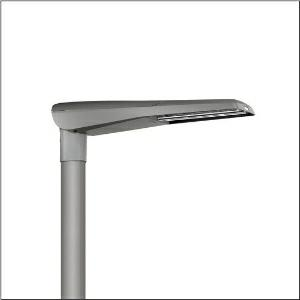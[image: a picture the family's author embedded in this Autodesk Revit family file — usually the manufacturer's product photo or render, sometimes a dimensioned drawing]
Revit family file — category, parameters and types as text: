
# Revit family: streetlight_sl_11_iq_mini___st0_5a_5xc2bc1f08ge_6b58
name_source: partatom
category: Lighting Fixtures
units: mm (PartAtom-declared; Revit-internal decimal feet)

## family parameters
Cut with Voids When Loaded = No
Host = Face
Light Source = No
Part Type = Normal
Room Calculation Point = No
Round Connector Dimension = Use Diameter
Shared = No

## types (1)
- --- (1 x LED, 3020 lm, 25.3 W, 2200K)
    Apparent Load = 25 VA
    CIE Flux Codes = 43 74 97 100 100
    Color Rendering = 70
    Color Temperature = 2200K
    Default Elevation = 1800 mm
    Description = Streetlight SL 11 iQ mini, mast luminaire, primary light control with 3 zone facetted reflector, of plastic, silver coated, highly specular, primary optical cover: cover, of PMMA, transparent, light distribution: ST0.5a, light emission: direct distribution, primary light characteristic: asymmetric, installation type: post-top, side-entry, lamps: LED, High Power LED, rated values: 3.550lm | 24,9W | 142,6lm/W (begin service life); end service life: 3.550lm | 25,7W; at 50% lumin. flux: 1.775lm | 12,8W | 138,7lm/W, colour temperature: 2200/2700/3000/4000K, colour rendering: CRI > 70, light colour: 722/727/730/740, light setting 1 begin service life: 100% | 3.550lm | 24,9W | 142,6lm/W | 3.000K, light setting 1 end service life: 25,7W, further light settings possible, control: Street-Remote, Auto-Match, Temp-Guard, Lumen-Switch, Night-Set, Smart-Wire, Light-Fading, Desk-Remote (wireless, voltage-free reading and setting of iQ features in the workshop via application-optimized NFC function/RFID function), optimised constant luminous flux control (CLO 2.0), with cable H07RN-F 5x 1.5mm², mains connection: 230..240V, AC, 50/60Hz, connection cable pre-assembled, cable length: 6,5m, luminaire housing, of diecast aluminium, powder-coated, Siteco® metallic grey (DB 702S), please order mast flange separately, inclination adjustable without tools: 0°, 5°, 10°, 15° (post-top) | 0°, -5°, -10°, -15° (side-entry), sealing non-destructively replaceable, multi-level sealing system, length: 736mm, width: 174mm, height: 116mm, mast flange for spigot size: 42mm (side-entry): 5XC10008XM4, 60/48mm (side-entry/post-top): 5XC10108XM2, 76/60mm (side-entry/post-top): 5XC10108XM1, equipment: standard, protection rating (complete): IP66, insulation class (complete): insulation class II (safety insulation), certification: CE, ENEC, ENEC+, VDE, impact resistance: IK10, permissible operating ambient temperature for outdoor applications: -25..+50°C, standard-compliant lighting for roads and squares, Environmental Product Declaration (EPD) tested and certified by an independent institute, packaging unit: 1 piece

Light Distribution: ST0.5a
    Height = 116 mm
    Lamp = 1 x LED
    Lamp Light Flux = 3020 lm
    Lamp Power = 25.3 W
    Lamp count = 1
    Length = 736 mm
    Luminous efficacy = 119 lm/W
    Manufacturer = Siteco
    ModVariant = No
    Model = 5XC2BC1F08GE
    Number of Poles = 1
    OnlyDefault = Yes
    Power Factor = 1
    Product Name = Streetlight SL 11 iQ mini | ST0.5a
    Product group = mast luminaire | pylon top
    ProductGroupID = 6100
    Protection Class = Protection class II
    Protection Degree = IP 66
    RLX_Detail_Level = 1
    RLX_Emergency_Light_Flux = 0 lm
    RLX_Emergency_Type = 0
    RLX_Emergency_Type_DB = No
    RlxData = <blob elided: 58021 chars, md5=802e574d>
    Socket = socket
    Standby Power = 0 W
    System Light Flux = 3020 lm
    System Power = 25 W
    Type Comments = individual setting: luminous flux: 100 % | dim-lin: 254 | 351 mA
    Type Image = l_1003508.jpg
    URL = http://relux.com
    VarID = @adj_035882
    Voltage = 0 V
    Weight = 0.00 kg
    Width = 174 mm

## geometry (parser evidence)
native form markers: Blend x4, Sweep x11
no freeform markers — native parametric forms only
